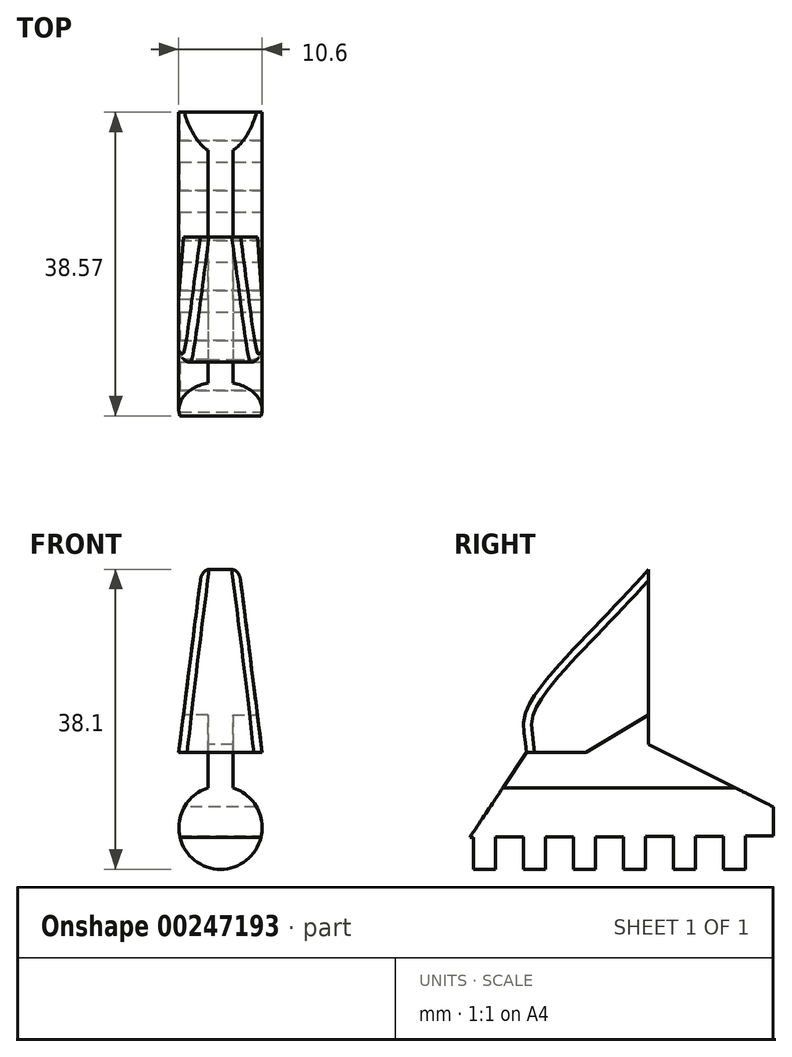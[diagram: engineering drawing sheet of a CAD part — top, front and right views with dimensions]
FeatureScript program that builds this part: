
annotation { "Feature Type Name" : "Feature", "Feature Type Description" : "" }
export const myFeature = defineFeature(function(context is Context, id is Id, definition is map)
    precondition{}
    {
        {
            var Q0;
            Q0=qCreatedBy(makeId("Right.planeOp"),FACE);
            var sketch = newSketch(context, id + "F0", { "sketchPlane" : qUnion([Q0])});
            skLineSegment(sketch, "E0", {"start": v(0, 0) * mm, "end": v(25.4, 38.1) * mm});
            skLineSegment(sketch, "E1", {"start": v(25.4, 38.1) * mm, "end": v(25.4, 15.88) * mm});
            skLineSegment(sketch, "E2", {"start": v(25.4, 15.88) * mm, "end": v(41.27, 7.94) * mm});
            skLineSegment(sketch, "E3", {"start": v(41.27, 7.94) * mm, "end": v(41.27, 0) * mm});
            skLineSegment(sketch, "E4", {"start": v(41.27, 0) * mm, "end": v(41.27, 0) * mm});
            skLineSegment(sketch, "E5", {"start": v(0, 0) * mm, "end": v(41.27, 0) * mm});
            skSolve(sketch);
        }
        {
            var Q0;
            Q0 = qSketchRegion(id + "F0", true);
            extrude(context, id + "F1", {"entities" : qUnion([Q0]), "depth" : 10.6 * mm, "symmetric" : true});
        }
        {
            var Q0;
            Q0=qCreatedBy(makeId("Front.planeOp"),FACE);
            var sketch = newSketch(context, id + "F10", { "sketchPlane" : qUnion([Q0])});
            skLineSegment(sketch, "E6.0.0", {"start": v(-5.3, 38.1) * mm, "end": v(-5.3, 0) * mm});
            skLineSegment(sketch, "E6.0.1", {"start": v(-5.3, 0) * mm, "end": v(5.3, 0) * mm});
            skLineSegment(sketch, "E6.0.2", {"start": v(5.3, 0) * mm, "end": v(5.3, 38.1) * mm});
            skLineSegment(sketch, "E6.0.3", {"start": v(5.3, 38.1) * mm, "end": v(-5.3, 38.1) * mm});
            skCircle(sketch, "E7", {"center": v(0, 5.3) * mm, "radius": 5.3 * mm});
            skPoint(sketch, "E7.first.point", {"position": v(0, 0) * mm});
            skPoint(sketch, "E7.second.point", {"position": v(5.3, 5.3) * mm});
            skPoint(sketch, "E7.third.point", {"position": v(-5.3, 5.3) * mm});
            skLineSegment(sketch, "E8", {"start": v(-1.59, 10.35) * mm, "end": v(-1.59, 14.82) * mm});
            skLineSegment(sketch, "E9", {"start": v(-1.59, 14.82) * mm, "end": v(-5.3, 14.82) * mm});
            skLineSegment(sketch, "E10", {"start": v(1.59, 10.35) * mm, "end": v(1.59, 14.82) * mm});
            skLineSegment(sketch, "E11", {"start": v(1.59, 14.82) * mm, "end": v(5.3, 14.82) * mm});
            skSolve(sketch);
        }
        {
            var Q0;
            {var subQ4=sQuery(id+"F10.wireOp",EDGE,"E8");Q0=makeQuery(id+"F10.imprint","IMPRINT",FACE,{"disambiguationData":[TD([[makeQuery(id+"F10.imprint","IMPRINT",EDGE,{"derivedFrom":subQ4}),1.0]])]});}
            var Q1;
            {var subQ4=sQuery(id+"F10.wireOp",EDGE,"E10");Q1=makeQuery(id+"F10.imprint","IMPRINT",FACE,{"disambiguationData":[TD([[makeQuery(id+"F10.imprint","IMPRINT",EDGE,{"derivedFrom":subQ4}),-1.0]])]});}
            var Q2;
            {var subQ0=sQuery(id+"F10.wireOp",EDGE,"E6.0.1");var subQ1=sQuery(id+"F10.wireOp",EDGE,"E6.0.0");var subQ2=makeQuery(id+"F10.imprint","INTERSECT",VERTEX,{"derivedFrom":[subQ1,subQ0]});Q2=makeQuery(id+"F10.imprint","IMPRINT",FACE,{"disambiguationData":[TD([[makeQuery(id+"F10.imprint","IMPRINT",EDGE,{"disambiguationData":[TD([[subQ2,1.0]])],"derivedFrom":subQ1}),1.0]])]});}
            var Q3;
            {var subQ0=sQuery(id+"F10.wireOp",EDGE,"E6.0.2");var subQ1=sQuery(id+"F10.wireOp",EDGE,"E6.0.1");var subQ2=makeQuery(id+"F10.imprint","INTERSECT",VERTEX,{"derivedFrom":[subQ1,subQ0]});Q3=makeQuery(id+"F10.imprint","IMPRINT",FACE,{"disambiguationData":[TD([[makeQuery(id+"F10.imprint","IMPRINT",EDGE,{"disambiguationData":[TD([[subQ2,1.0]])],"derivedFrom":subQ1}),1.0]])]});}
            extrude(context, id + "F2", {"entities" : qUnion([Q0, Q1, Q2, Q3]), "operationType" : NewBodyOperationType.REMOVE, "endBound" : BoundingType.THROUGH_ALL, "oppositeDirection" : true, "depth" : 25.4 * mm});
        }
        {
            var Q0;
            Q0=makeQuery(id+"F1.opExtrude","CAP_FACE",FACE,{"disambiguationData":[OSD([sQuery(id+"F0.wireOp",EDGE,"E0"),sQuery(id+"F0.wireOp",EDGE,"E1"),sQuery(id+"F0.wireOp",EDGE,"E2"),sQuery(id+"F0.wireOp",EDGE,"E3"),sQuery(id+"F0.wireOp",EDGE,"E5")])],"isStart":false});
            var sketch = newSketch(context, id + "F3", { "sketchPlane" : qUnion([Q0])});
            skLineSegment(sketch, "E12.0", {"start": v(27.5, 14.82) * mm, "end": v(9.88, 14.82) * mm});
            skLineSegment(sketch, "E13.0", {"start": v(25.4, 38.1) * mm, "end": v(25.4, 15.88) * mm});
            skLineSegment(sketch, "E14.0", {"start": v(25.4, 15.88) * mm, "end": v(27.5, 14.82) * mm});
            skLineSegment(sketch, "E15", {"start": v(17.46, 14.82) * mm, "end": v(25.4, 19.58) * mm});
            skSolve(sketch);
        }
        {
            var Q0;
            {var subQ0=sQuery(id+"F3.wireOp",EDGE,"E14.0");Q0=makeQuery(id+"F3.imprint","IMPRINT",FACE,{"disambiguationData":[TD([[makeQuery(id+"F3.imprint","IMPRINT",EDGE,{"derivedFrom":subQ0}),-1.0]])]});}
            extrude(context, id + "F4", {"entities" : qUnion([Q0]), "operationType" : NewBodyOperationType.REMOVE, "oppositeDirection" : true, "depth" : 3.7 * mm});
        }
        {
            var Q0;
            Q0=makeQuery(id+"F1.opExtrude","CAP_FACE",FACE,{"disambiguationData":[OSD([sQuery(id+"F0.wireOp",EDGE,"E0"),sQuery(id+"F0.wireOp",EDGE,"E1"),sQuery(id+"F0.wireOp",EDGE,"E2"),sQuery(id+"F0.wireOp",EDGE,"E3"),sQuery(id+"F0.wireOp",EDGE,"E5")])],"isStart":true});
            var sketch = newSketch(context, id + "F11", { "sketchPlane" : qUnion([Q0])});
            skLineSegment(sketch, "E16.0", {"start": v(-17.46, 14.82) * mm, "end": v(-25.4, 19.58) * mm});
            skSolve(sketch);
        }
        {
            var Q0;
            {var subQ0=sQuery(id+"F11.wireOp",EDGE,"E16.0");Q0=makeQuery(id+"F11.imprint","IMPRINT",FACE,{"disambiguationData":[TD([[makeQuery(id+"F11.imprint","IMPRINT",EDGE,{"derivedFrom":subQ0}),1.0]])]});}
            extrude(context, id + "F12", {"entities" : qUnion([Q0]), "operationType" : NewBodyOperationType.REMOVE, "oppositeDirection" : true, "depth" : 3.7 * mm});
        }
        {
            var Q0;
            Q0=makeQuery(id+"F1.opExtrude","CAP_FACE",FACE,{"disambiguationData":[OSD([sQuery(id+"F0.wireOp",EDGE,"E0"),sQuery(id+"F0.wireOp",EDGE,"E1"),sQuery(id+"F0.wireOp",EDGE,"E2"),sQuery(id+"F0.wireOp",EDGE,"E3"),sQuery(id+"F0.wireOp",EDGE,"E5")])],"isStart":false});
            var sketch = newSketch(context, id + "F5", { "sketchPlane" : qUnion([Q0])});
            skFitSpline(sketch, "E17", {"points": [v(9.88, 14.82) * mm, v(9.88, 20.16) * mm, v(25.4, 38.1) * mm], "startDerivative": vector(-0.86, 20.32) * mm, "endDerivative": vector(28.4, 32.28) * mm});
            skSolve(sketch);
        }
        {
            var Q0;
            Q0=makeQuery(id+"F5.imprint","IMPRINT",FACE,{"disambiguationData":[TD([[makeQuery(id+"F5.imprint","IMPRINT",EDGE,{"derivedFrom":sQuery(id+"F5.wireOp",EDGE,"E17")}),-1.0]])]});
            extrude(context, id + "F6", {"entities" : qUnion([Q0]), "operationType" : NewBodyOperationType.ADD, "oppositeDirection" : true, "depth" : 10.6 * mm});
        }
        {
            var Q0;
            Q0=qCreatedBy(makeId("Front.planeOp"),FACE);
            var sketch = newSketch(context, id + "F13", { "sketchPlane" : qUnion([Q0])});
            skLineSegment(sketch, "E18.0", {"start": v(1.59, 14.82) * mm, "end": v(5.3, 14.82) * mm});
            skLineSegment(sketch, "E19.0", {"start": v(-1.59, 14.82) * mm, "end": v(-5.3, 14.82) * mm});
            skLineSegment(sketch, "E20.0", {"start": v(-1.59, 14.82) * mm, "end": v(1.59, 14.82) * mm});
            skLineSegment(sketch, "E21.0", {"start": v(5.3, 38.1) * mm, "end": v(-5.3, 38.1) * mm});
            skLineSegment(sketch, "E22", {"start": v(-5.3, 14.82) * mm, "end": v(-2.38, 38.1) * mm});
            skLineSegment(sketch, "E23", {"start": v(5.3, 14.82) * mm, "end": v(2.38, 38.1) * mm});
            skFitSpline(sketch, "E24.0", {"points": [v(5.3, 14.82) * mm, v(5.3, 17) * mm, v(5.3, 20.97) * mm, v(5.3, 30.8) * mm, v(5.3, 38.1) * mm]});
            skFitSpline(sketch, "E25.0", {"points": [v(-5.3, 14.82) * mm, v(-5.3, 17) * mm, v(-5.3, 20.97) * mm, v(-5.3, 30.8) * mm, v(-5.3, 38.1) * mm]});
            skSolve(sketch);
        }
        {
            var Q0;
            {var subQ2=sQuery(id+"F13.wireOp",EDGE,"E22");Q0=makeQuery(id+"F13.imprint","IMPRINT",FACE,{"disambiguationData":[TD([[makeQuery(id+"F13.imprint","IMPRINT",EDGE,{"derivedFrom":subQ2}),1.0]])]});}
            var Q1;
            {var subQ2=sQuery(id+"F13.wireOp",EDGE,"E23");Q1=makeQuery(id+"F13.imprint","IMPRINT",FACE,{"disambiguationData":[TD([[makeQuery(id+"F13.imprint","IMPRINT",EDGE,{"derivedFrom":subQ2}),-1.0]])]});}
            extrude(context, id + "F7", {"entities" : qUnion([Q0, Q1]), "operationType" : NewBodyOperationType.REMOVE, "endBound" : BoundingType.THROUGH_ALL, "oppositeDirection" : true, "depth" : 25.4 * mm});
        }
        {
            var Q0;
            Q0=qCreatedBy(makeId("Right.planeOp"),FACE);
            var sketch = newSketch(context, id + "F8", { "sketchPlane" : qUnion([Q0])});
            skLineSegment(sketch, "E26", {"start": v(41.28, 0) * mm, "end": v(0, 0) * mm});
            skLineSegment(sketch, "E27.0", {"start": v(41.27, 7.94) * mm, "end": v(41.27, 0) * mm});
            skLineSegment(sketch, "E28", {"start": v(41.28, 0) * mm, "end": v(37.7, 0) * mm});
            skLineSegment(sketch, "E29", {"start": v(37.7, 0) * mm, "end": v(37.7, 4.23) * mm});
            skLineSegment(sketch, "E30", {"start": v(37.7, 4.23) * mm, "end": v(41.27, 4.23) * mm});
            skLineSegment(sketch, "E31", {"start": v(41.27, 4.23) * mm, "end": v(41.28, 0) * mm});
            skLineSegment(sketch, "E32.1.0.0", {"start": v(34.93, 4.2) * mm, "end": v(34.93, -0.03) * mm});
            skLineSegment(sketch, "E32.1.0.1", {"start": v(31.36, 4.2) * mm, "end": v(34.93, 4.2) * mm});
            skLineSegment(sketch, "E32.1.0.2", {"start": v(31.36, -0.03) * mm, "end": v(31.36, 4.2) * mm});
            skLineSegment(sketch, "E32.2.0.0", {"start": v(28.58, 4.17) * mm, "end": v(28.58, -0.05) * mm});
            skLineSegment(sketch, "E32.2.0.1", {"start": v(25, 4.17) * mm, "end": v(28.58, 4.17) * mm});
            skLineSegment(sketch, "E32.2.0.2", {"start": v(25, -0.05) * mm, "end": v(25, 4.17) * mm});
            skLineSegment(sketch, "E32.3.0.0", {"start": v(22.23, 4.15) * mm, "end": v(22.23, -0.08) * mm});
            skLineSegment(sketch, "E32.3.0.1", {"start": v(18.66, 4.15) * mm, "end": v(22.23, 4.15) * mm});
            skLineSegment(sketch, "E32.3.0.2", {"start": v(18.66, -0.08) * mm, "end": v(18.66, 4.15) * mm});
            skLineSegment(sketch, "E32.4.0.0", {"start": v(15.88, 4.12) * mm, "end": v(15.88, -0.1) * mm});
            skLineSegment(sketch, "E32.4.0.1", {"start": v(12.3, 4.12) * mm, "end": v(15.88, 4.12) * mm});
            skLineSegment(sketch, "E32.4.0.2", {"start": v(12.3, -0.1) * mm, "end": v(12.3, 4.12) * mm});
            skLineSegment(sketch, "E32.5.0.0", {"start": v(9.53, 4.1) * mm, "end": v(9.53, -0.14) * mm});
            skLineSegment(sketch, "E32.5.0.1", {"start": v(5.96, 4.1) * mm, "end": v(9.53, 4.1) * mm});
            skLineSegment(sketch, "E32.5.0.2", {"start": v(5.96, -0.14) * mm, "end": v(5.96, 4.1) * mm});
            skLineSegment(sketch, "E32.6.0.0", {"start": v(3.18, 4.07) * mm, "end": v(3.18, -0.16) * mm});
            skLineSegment(sketch, "E32.6.0.1", {"start": v(-0.4, 4.07) * mm, "end": v(3.18, 4.07) * mm});
            skLineSegment(sketch, "E32.6.0.2", {"start": v(-0.4, -0.16) * mm, "end": v(-0.4, 4.07) * mm});
            skLineSegment(sketch, "E32.direction1", {"start": v(41.28, 0) * mm, "end": v(34.93, -0.03) * mm, "construction": true});
            skLineSegment(sketch, "E33", {"start": v(-0.4, -0.16) * mm, "end": v(3.18, -0.16) * mm});
            skLineSegment(sketch, "E34", {"start": v(5.96, -0.14) * mm, "end": v(9.53, -0.14) * mm});
            skLineSegment(sketch, "E35", {"start": v(12.3, -0.1) * mm, "end": v(15.88, -0.1) * mm});
            skLineSegment(sketch, "E36", {"start": v(18.66, -0.08) * mm, "end": v(22.23, -0.08) * mm});
            skLineSegment(sketch, "E37", {"start": v(25, -0.05) * mm, "end": v(28.58, -0.05) * mm});
            skLineSegment(sketch, "E38", {"start": v(31.36, -0.03) * mm, "end": v(34.93, -0.03) * mm});
            skLineSegment(sketch, "E39", {"start": v(37.7, 0) * mm, "end": v(41.28, 0) * mm});
            skSolve(sketch);
        }
        {
            var Q0;
            Q0 = qSketchRegion(id + "F8", true);
            extrude(context, id + "F14", {"entities" : qUnion([Q0]), "operationType" : NewBodyOperationType.REMOVE, "oppositeDirection" : true, "depth" : 25.4 * mm, "symmetric" : true});
        }
        {
            var Q0;
            Q0=makeQuery(id+"F7.boolean.opBoolean","INTERSECT",EDGE,{"derivedFrom":[makeQuery(id+"F6.opExtrude","SWEPT_FACE",FACE,{"disambiguationData":[OSD([sQuery(id+"F5.wireOp",EDGE,"E17")])]}),makeQuery(id+"F7.opExtrude","SWEPT_FACE",FACE,{"disambiguationData":[OSD([sQuery(id+"F13.wireOp",EDGE,"E23")])]})]});
            var Q1;
            Q1=makeQuery(id+"F7.boolean.opBoolean","INTERSECT",EDGE,{"derivedFrom":[makeQuery(id+"F6.opExtrude","SWEPT_FACE",FACE,{"disambiguationData":[OSD([sQuery(id+"F5.wireOp",EDGE,"E17")])]}),makeQuery(id+"F7.opExtrude","SWEPT_FACE",FACE,{"disambiguationData":[OSD([sQuery(id+"F13.wireOp",EDGE,"E22")])]})]});
            fillet(context, id + "F9", {"entities" : qUnion([Q0, Q1]), "radius" : 1.02 * mm, "tangentPropagation" : true, "allowEdgeOverflow" : false});
        }
    });
